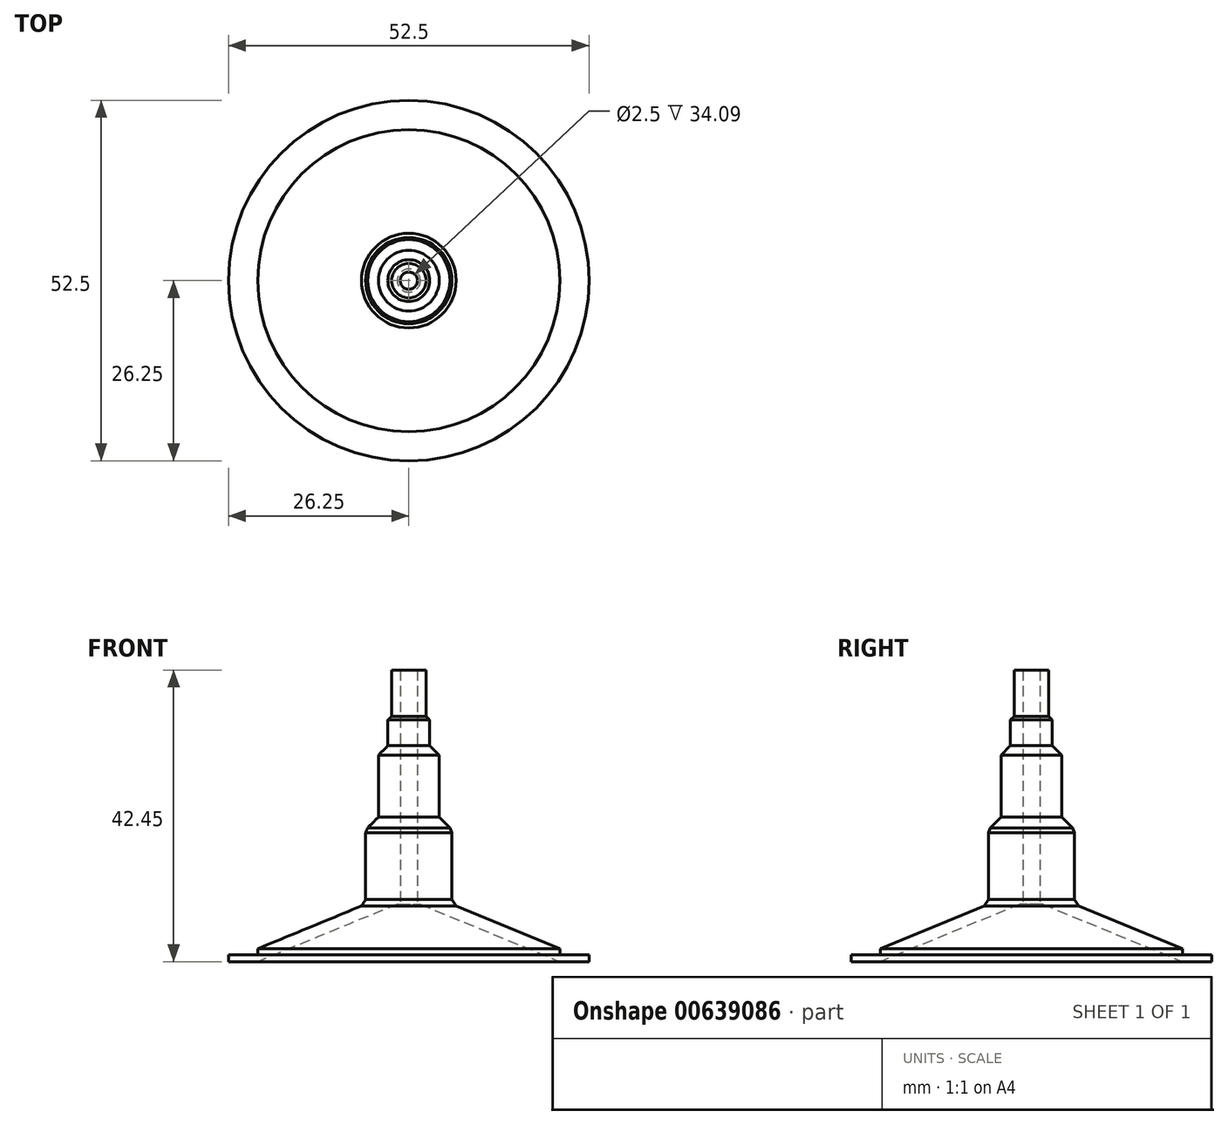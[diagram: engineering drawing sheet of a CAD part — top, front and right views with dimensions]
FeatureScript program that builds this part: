
annotation { "Feature Type Name" : "Feature", "Feature Type Description" : "" }
export const myFeature = defineFeature(function(context is Context, id is Id, definition is map)
    precondition{}
    {
        {
            var Q0;
            Q0=qCreatedBy(makeId("Front.planeOp"),FACE);
            var sketch = newSketch(context, id + "F0", { "sketchPlane" : qUnion([Q0])});
            skLineSegment(sketch, "E0.bottom", {"start": v(0, 0) * mm, "end": v(-6.28, 0) * mm});
            skLineSegment(sketch, "E0.top", {"start": v(0, 12.84) * mm, "end": v(-6.28, 12.84) * mm});
            skLineSegment(sketch, "E0.left", {"start": v(0, 0) * mm, "end": v(0, 12.84) * mm});
            skLineSegment(sketch, "E0.right", {"start": v(-6.28, 0) * mm, "end": v(-6.28, 12.84) * mm});
            skLineSegment(sketch, "E1.bottom", {"start": v(0, 12.84) * mm, "end": v(-4.42, 12.84) * mm});
            skLineSegment(sketch, "E1.top", {"start": v(0, 21.59) * mm, "end": v(-4.42, 21.59) * mm});
            skLineSegment(sketch, "E1.left", {"start": v(0, 12.84) * mm, "end": v(0, 21.59) * mm});
            skLineSegment(sketch, "E1.right", {"start": v(-4.42, 12.84) * mm, "end": v(-4.42, 21.59) * mm});
            skLineSegment(sketch, "E2.bottom", {"start": v(0, 21.59) * mm, "end": v(-3.05, 21.59) * mm});
            skLineSegment(sketch, "E2.top", {"start": v(0, 28.34) * mm, "end": v(-3.05, 28.34) * mm});
            skLineSegment(sketch, "E2.left", {"start": v(0, 21.59) * mm, "end": v(0, 28.34) * mm});
            skLineSegment(sketch, "E2.right", {"start": v(-3.05, 21.59) * mm, "end": v(-3.05, 28.34) * mm});
            skLineSegment(sketch, "E3.bottom", {"start": v(0, 28.34) * mm, "end": v(-2.5, 28.34) * mm});
            skLineSegment(sketch, "E3.top", {"start": v(0, 34.09) * mm, "end": v(-2.5, 34.09) * mm});
            skLineSegment(sketch, "E3.left", {"start": v(0, 28.34) * mm, "end": v(0, 34.09) * mm});
            skLineSegment(sketch, "E3.right", {"start": v(-2.5, 28.34) * mm, "end": v(-2.5, 34.09) * mm});
            skLineSegment(sketch, "E4", {"start": v(-6.28, 0) * mm, "end": v(-22, -6.47) * mm});
            skLineSegment(sketch, "E5", {"start": v(-22, -6.47) * mm, "end": v(-22, -8.36) * mm});
            skLineSegment(sketch, "E6", {"start": v(-22, -8.36) * mm, "end": v(-1.68, 0) * mm});
            skLineSegment(sketch, "E7", {"start": v(-26.25, -8.36) * mm, "end": v(-22, -8.36) * mm});
            skLineSegment(sketch, "E8", {"start": v(-26.25, -8.36) * mm, "end": v(-26.25, -7.36) * mm});
            skLineSegment(sketch, "E9", {"start": v(-26.25, -7.36) * mm, "end": v(-22, -7.36) * mm});
            skSolve(sketch);
        }
        {
            var Q0;
            Q0=qSketchRegion(id+"F0",true);
            var Q1;
            Q1=sQuery(id+"F0.wireOp",EDGE,"E0.left");
            revolve(context, id + "F1", {"entities" : qUnion([Q0]), "axis" : qUnion([Q1]), "revolveType" : RevolveType.FULL});
        }
        {
            var Q0;
            Q0=makeQuery(id+"F1.opRevolve","SWEPT_FACE",FACE,{"disambiguationData":[OSD([sQuery(id+"F0.wireOp",EDGE,"E2.right")])]});
            chamfer(context, id + "F2", {"entities" : qUnion([Q0]), "chamferType" : ChamferType.OFFSET_ANGLE, "width" : 1.5 * mm, "oppositeDirection" : false, "angle" : 45 * degree, "tangentPropagation" : true});
        }
        {
            var Q0;
            Q0=makeQuery(id+"F1.opRevolve","SWEPT_EDGE",EDGE,{"disambiguationData":[OSD([sQuery(id+"F0.wireOp",EDGE,"E0.top"),sQuery(id+"F0.wireOp",EDGE,"E0.right")])]});
            chamfer(context, id + "F3", {"entities" : qUnion([Q0]), "width" : 2 * mm, "tangentPropagation" : true});
        }
        {
            var Q0;
            Q0=makeQuery(id+"F1.opRevolve","SWEPT_FACE",FACE,{"disambiguationData":[OSD([sQuery(id+"F0.wireOp",EDGE,"E0.right")])]});
            chamfer(context, id + "F4", {"entities" : qUnion([Q0]), "width" : 1 * mm, "tangentPropagation" : true});
        }
        {
            var Q0;
            Q0=qCreatedBy(makeId("Top.planeOp"),FACE);
            var sketch = newSketch(context, id + "F5", { "sketchPlane" : qUnion([Q0])});
            skCircle(sketch, "E10", {"center": v(0, 0) * mm, "radius": 1.25 * mm});
            skSolve(sketch);
        }
        {
            var Q0;
            Q0=qSketchRegion(id+"F5",true);
            extrude(context, id + "F6", {"entities" : qUnion([Q0]), "operationType" : NewBodyOperationType.REMOVE, "endBound" : BoundingType.THROUGH_ALL, "depth" : 25 * mm, "hasSecondDirection" : true, "secondDirectionBound" : SecondDirectionBoundingType.THROUGH_ALL, "secondDirectionOppositeDirection" : true, "secondDirectionDepth" : 25 * mm});
        }
    });
